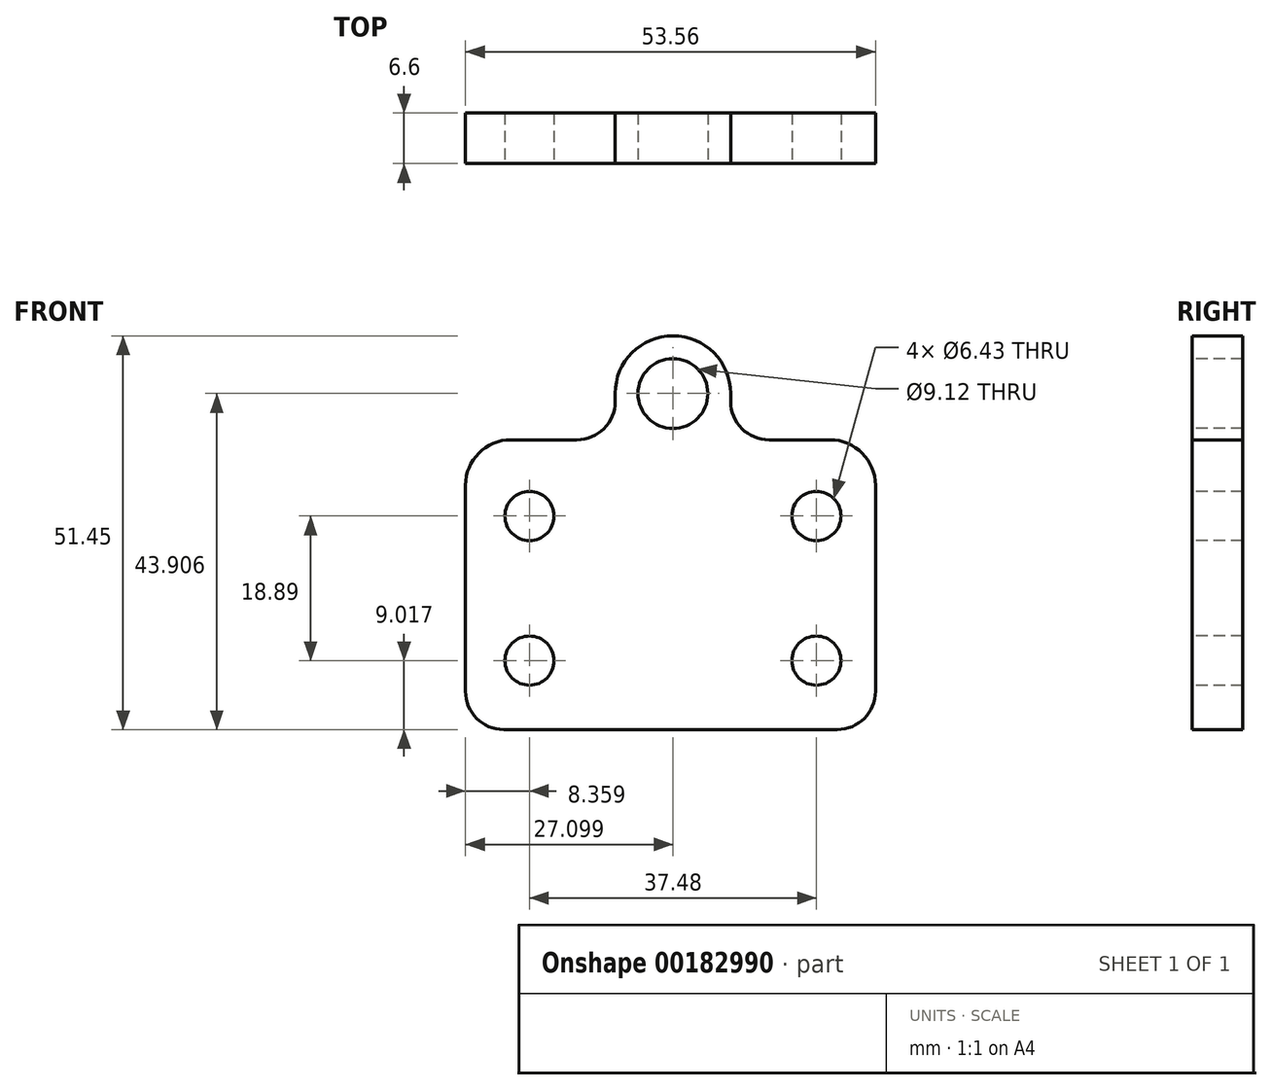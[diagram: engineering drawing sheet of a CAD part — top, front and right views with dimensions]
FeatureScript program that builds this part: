
annotation { "Feature Type Name" : "Feature", "Feature Type Description" : "" }
export const myFeature = defineFeature(function(context is Context, id is Id, definition is map)
    precondition{}
    {
        {
            var Q0;
            Q0=qCreatedBy(makeId("Front.planeOp"),FACE);
            var sketch = newSketch(context, id + "F0", { "sketchPlane" : qUnion([Q0])});
            skLineSegment(sketch, "E0.bottom", {"start": v(-5, 0) * mm, "end": v(-48.56, 0) * mm});
            skLineSegment(sketch, "E0.top", {"start": v(-5.94, 37.87) * mm, "end": v(-13.91, 37.87) * mm});
            skLineSegment(sketch, "E0.left", {"start": v(0, 5) * mm, "end": v(0, 31.92) * mm});
            skLineSegment(sketch, "E0.right", {"start": v(-53.56, 5) * mm, "end": v(-53.56, 31.92) * mm});
            skPoint(sketch, "E1", {"position": v(-58.22, 44.67) * mm});
            skPoint(sketch, "E2", {"position": v(-58.22, -8.25) * mm});
            skPoint(sketch, "E3", {"position": v(7.5, -8.25) * mm});
            skPoint(sketch, "E4", {"position": v(7.5, 44.67) * mm});
            skLineSegment(sketch, "E5.trimOffspring", {"start": v(-39, 37.87) * mm, "end": v(-47.62, 37.87) * mm});
            skArc(sketch, "E6.filletArc", {"start": v(-47.62, 37.87) * mm, "mid": v(-51.82, 36.13) * mm, "end": v(-53.56, 31.92) * mm});
            skPoint(sketch, "E7.visualSharp", {"position": v(-53.56, 0) * mm});
            skArc(sketch, "E7.filletArc", {"start": v(-53.56, 5) * mm, "mid": v(-52.1, 1.46) * mm, "end": v(-48.56, 0) * mm});
            skPoint(sketch, "E8.visualSharp", {"position": v(0, 0) * mm});
            skArc(sketch, "E8.filletArc", {"start": v(-5, 0) * mm, "mid": v(-1.46, 1.46) * mm, "end": v(0, 5) * mm});
            skArc(sketch, "E9.filletArc", {"start": v(0, 31.92) * mm, "mid": v(-1.74, 36.13) * mm, "end": v(-5.94, 37.87) * mm});
            skLineSegment(sketch, "E10", {"start": v(-34, 42.87) * mm, "end": v(-34, 43.9) * mm});
            skLineSegment(sketch, "E11", {"start": v(-18.91, 42.87) * mm, "end": v(-18.91, 43.9) * mm});
            skArc(sketch, "E12", {"start": v(-18.91, 43.9) * mm, "mid": v(-26.46, 51.45) * mm, "end": v(-34, 43.9) * mm});
            skCircle(sketch, "E13", {"center": v(-26.46, 43.9) * mm, "radius": 4.56 * mm});
            skPoint(sketch, "E14.visualSharp", {"position": v(-34, 37.87) * mm});
            skArc(sketch, "E14.filletArc", {"start": v(-39, 37.87) * mm, "mid": v(-35.47, 39.33) * mm, "end": v(-34, 42.87) * mm});
            skPoint(sketch, "E15.visualSharp", {"position": v(-18.91, 37.87) * mm});
            skArc(sketch, "E15.filletArc", {"start": v(-18.91, 42.87) * mm, "mid": v(-17.45, 39.33) * mm, "end": v(-13.91, 37.87) * mm});
            skCircle(sketch, "E16", {"center": v(-45.2, 27.9) * mm, "radius": 3.21 * mm});
            skCircle(sketch, "E17.MirrorC", {"center": v(-45.2, 9.02) * mm, "radius": 3.21 * mm});
            skCircle(sketch, "E18.MirrorC", {"center": v(-7.72, 27.9) * mm, "radius": 3.21 * mm});
            skCircle(sketch, "E19.MirrorC", {"center": v(-7.72, 9.02) * mm, "radius": 3.21 * mm});
            skSolve(sketch);
        }
        {
            var Q0;
            Q0=makeQuery(id+"F0.imprint","IMPRINT",FACE,{"disambiguationData":[TD([[makeQuery(id+"F0.imprint","IMPRINT",EDGE,{"derivedFrom":sQuery(id+"F0.wireOp",EDGE,"E0.bottom")}),-1.0]])]});
            extrude(context, id + "F1", {"entities" : qUnion([Q0]), "oppositeDirection" : true, "depth" : 6.6 * mm});
        }
    });
